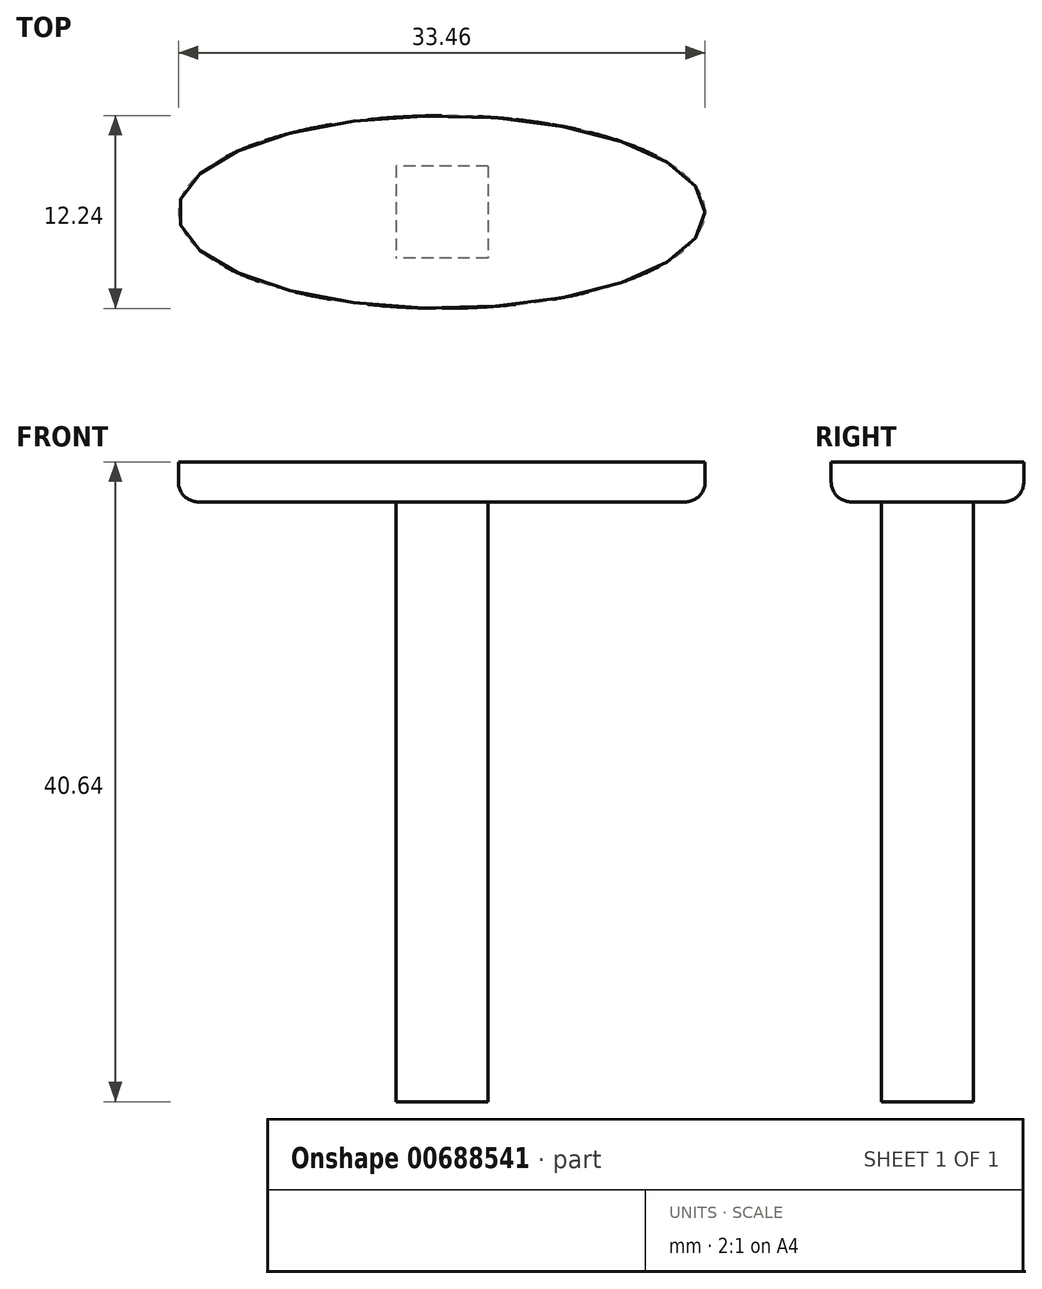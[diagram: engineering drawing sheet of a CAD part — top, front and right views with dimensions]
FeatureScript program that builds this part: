
annotation { "Feature Type Name" : "Feature", "Feature Type Description" : "" }
export const myFeature = defineFeature(function(context is Context, id is Id, definition is map)
    precondition{}
    {
        {
            var Q0;
            Q0=qCreatedBy(makeId("Top.planeOp"),FACE);
            var sketch = newSketch(context, id + "F0", { "sketchPlane" : qUnion([Q0])});
            skLineSegment(sketch, "E0.bottom", {"start": v(2.92, 2.92) * mm, "end": v(-2.92, 2.92) * mm});
            skLineSegment(sketch, "E0.top", {"start": v(2.92, -2.92) * mm, "end": v(-2.92, -2.92) * mm});
            skLineSegment(sketch, "E0.left", {"start": v(2.92, 2.92) * mm, "end": v(2.92, -2.92) * mm});
            skLineSegment(sketch, "E0.right", {"start": v(-2.92, 2.92) * mm, "end": v(-2.92, -2.92) * mm});
            skPoint(sketch, "E0.middle", {"position": v(0, 0) * mm});
            skSolve(sketch);
        }
        {
            var Q0;
            Q0=qSketchRegion(id+"F0",true);
            extrude(context, id + "F1", {"entities" : qUnion([Q0]), "depth" : 38.1 * mm, "offsetDistance" : 25.4 * mm});
        }
        {
            var Q0;
            Q0=makeQuery(id+"F1.opExtrude","CAP_FACE",FACE,{"disambiguationData":[OSD([sQuery(id+"F0.wireOp",EDGE,"E0.bottom"),sQuery(id+"F0.wireOp",EDGE,"E0.top"),sQuery(id+"F0.wireOp",EDGE,"E0.left"),sQuery(id+"F0.wireOp",EDGE,"E0.right")])],"isStart":false});
            var sketch = newSketch(context, id + "F2", { "sketchPlane" : qUnion([Q0])});
            skEllipse(sketch, "E1", {"center": v(0, 0) * mm, "majorRadius": 16.73 * mm, "minorRadius": 6.12 * mm, "majorAxis": v(1, 0)});
            skSolve(sketch);
        }
        {
            var Q0;
            Q0=qSketchRegion(id+"F2",true);
            extrude(context, id + "F3", {"entities" : qUnion([Q0]), "operationType" : NewBodyOperationType.ADD, "depth" : 2.54 * mm, "offsetDistance" : 25.4 * mm});
        }
        {
            var Q0;
            Q0=makeQuery(id+"F1.opExtrude","CAP_EDGE",EDGE,{"disambiguationData":[OSD([sQuery(id+"F0.wireOp",EDGE,"E0.left")])],"isStart":false});
            var Q1;
            Q1=makeQuery(id+"F1.opExtrude","CAP_EDGE",EDGE,{"disambiguationData":[OSD([sQuery(id+"F0.wireOp",EDGE,"E0.top")])],"isStart":false});
            var Q2;
            Q2=makeQuery(id+"F1.opExtrude","CAP_EDGE",EDGE,{"disambiguationData":[OSD([sQuery(id+"F0.wireOp",EDGE,"E0.right")])],"isStart":false});
            var Q3;
            Q3=makeQuery(id+"F1.opExtrude","CAP_EDGE",EDGE,{"disambiguationData":[OSD([sQuery(id+"F0.wireOp",EDGE,"E0.bottom")])],"isStart":false});
            var Q4;
            Q4=makeQuery(id+"F3.opExtrude","CAP_EDGE",EDGE,{"disambiguationData":[OSD([sQuery(id+"F2.wireOp",EDGE,"E1")])],"isStart":true});
            fillet(context, id + "F4", {"entities" : qUnion([Q0, Q1, Q2, Q3, Q4]), "radius" : 1.27 * mm, "tangentPropagation" : true, "allowEdgeOverflow" : false});
        }
    });
